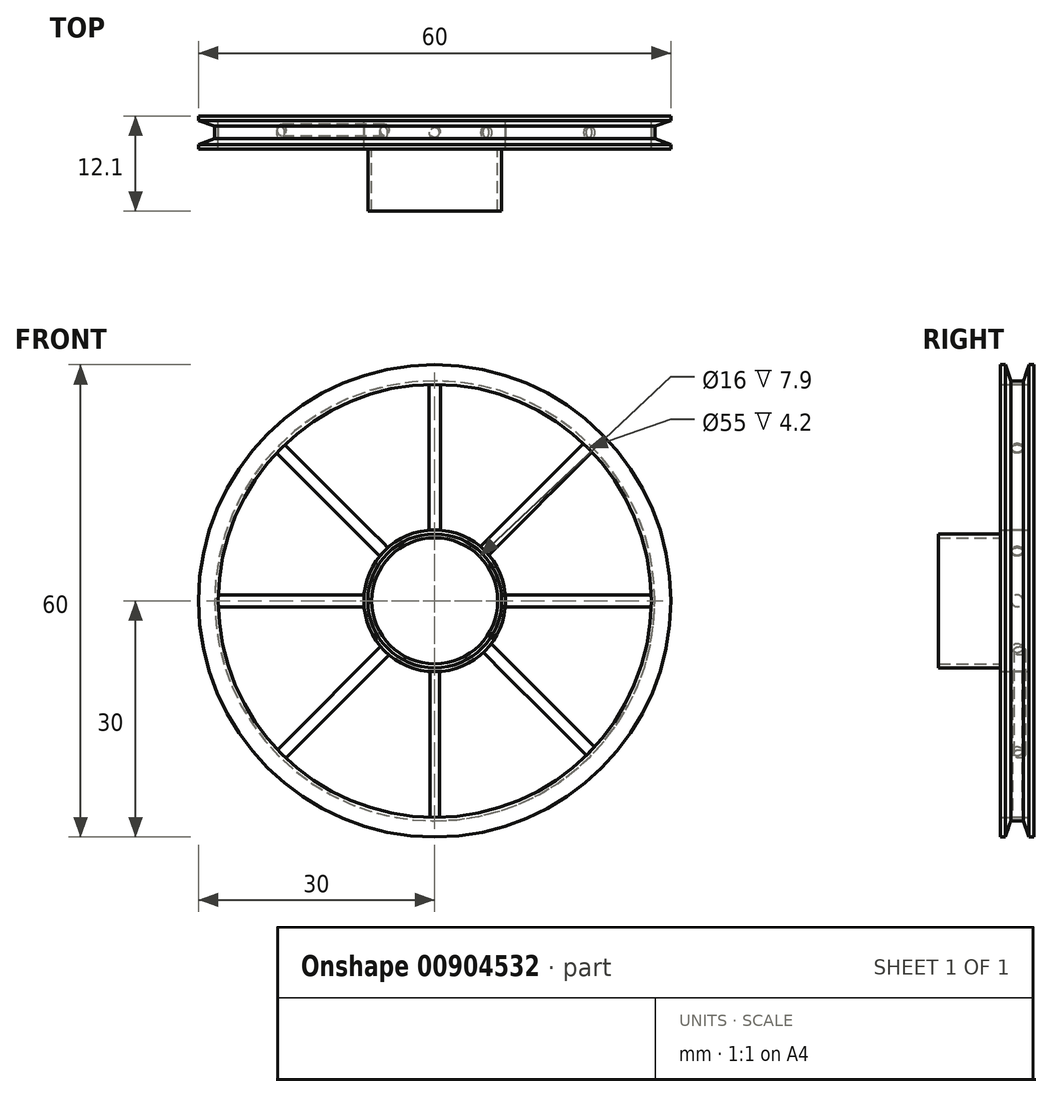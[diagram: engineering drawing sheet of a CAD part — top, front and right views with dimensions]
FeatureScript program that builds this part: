
annotation { "Feature Type Name" : "Feature", "Feature Type Description" : "" }
export const myFeature = defineFeature(function(context is Context, id is Id, definition is map)
    precondition{}
    {
        {
            var Q0;
            Q0=qCreatedBy(makeId("Front.planeOp"),FACE);
            var sketch = newSketch(context, id + "F0", { "sketchPlane" : qUnion([Q0])});
            skCircle(sketch, "E0", {"center": v(0, 0) * mm, "radius": 30 * mm});
            skCircle(sketch, "E1", {"center": v(0, 0) * mm, "radius": 27.5 * mm});
            skSolve(sketch);
        }
        {
            var Q0;
            Q0=qSketchRegion(id+"F0",true);
            extrude(context, id + "F1", {"entities" : qUnion([Q0]), "depth" : 2.1 * mm, "offsetDistance" : 25 * mm});
        }
        {
            var Q0;
            Q0=makeQuery(id+"F1.opExtrude","SWEPT_BODY",BODY,{"disambiguationData":[OSD([sQuery(id+"F0.wireOp",EDGE,"E0"),sQuery(id+"F0.wireOp",EDGE,"E1")])]});
            var Q1;
            Q1=qCreatedBy(makeId("Front.planeOp"),FACE);
            mirror(context, id + "F2", {"operationType" : NewBodyOperationType.ADD, "entities" : qUnion([Q0]), "mirrorPlane" : qUnion([Q1])});
        }
        {
            var Q0;
            Q0=qCreatedBy(makeId("Front.planeOp"),FACE);
            var sketch = newSketch(context, id + "F3", { "sketchPlane" : qUnion([Q0])});
            skCircle(sketch, "E2", {"center": v(0, 0) * mm, "radius": 8 * mm});
            skCircle(sketch, "E3", {"center": v(0, 0) * mm, "radius": 8.5 * mm});
            skSolve(sketch);
        }
        {
            var Q0;
            Q0=qSketchRegion(id+"F3",true);
            extrude(context, id + "F4", {"entities" : qUnion([Q0]), "depth" : 10 * mm, "offsetDistance" : 25 * mm});
        }
        {
            var Q0;
            Q0=qCreatedBy(makeId("Front.planeOp"),FACE);
            var sketch = newSketch(context, id + "F5", { "sketchPlane" : qUnion([Q0])});
            skCircle(sketch, "E4", {"center": v(0, 0) * mm, "radius": 9 * mm});
            skSolve(sketch);
        }
        {
            var Q0;
            Q0=makeQuery(id+"F5.imprint","IMPRINT",FACE,{"disambiguationData":[TD([[makeQuery(id+"F5.imprint","IMPRINT",EDGE,{"derivedFrom":sQuery(id+"F5.wireOp",EDGE,"E4")}),1.0]])]});
            extrude(context, id + "F6", {"entities" : qUnion([Q0]), "operationType" : NewBodyOperationType.ADD, "depth" : 2.1 * mm, "offsetDistance" : 25 * mm});
        }
        {
            var Q0;
            Q0=qCreatedBy(makeId("Front.planeOp"),FACE);
            var sketch = newSketch(context, id + "F7", { "sketchPlane" : qUnion([Q0])});
            skCircle(sketch, "E5", {"center": v(0, 0) * mm, "radius": 9 * mm});
            skSolve(sketch);
        }
        {
            var Q0;
            Q0=qSketchRegion(id+"F7",true);
            extrude(context, id + "F8", {"entities" : qUnion([Q0]), "operationType" : NewBodyOperationType.ADD, "oppositeDirection" : true, "depth" : 2.1 * mm, "offsetDistance" : 25 * mm});
        }
        {
            var Q0;
            Q0=qCreatedBy(makeId("Right.planeOp"),FACE);
            var sketch = newSketch(context, id + "F9", { "sketchPlane" : qUnion([Q0])});
            skLineSegment(sketch, "E6", {"start": v(1.7, -30.55) * mm, "end": v(-1.7, -30.55) * mm});
            skLineSegment(sketch, "E7", {"start": v(-1.7, -30.55) * mm, "end": v(-0.8, -27.95) * mm});
            skLineSegment(sketch, "E8", {"start": v(-0.8, -27.95) * mm, "end": v(0.8, -27.95) * mm});
            skLineSegment(sketch, "E9", {"start": v(0.8, -27.95) * mm, "end": v(1.7, -30.55) * mm});
            skLineSegment(sketch, "E10", {"start": v(0, -27.95) * mm, "end": v(0, -30.55) * mm});
            skLineSegment(sketch, "E11", {"start": v(0, 0) * mm, "end": v(-3.18, 0) * mm});
            skSolve(sketch);
        }
        {
            var Q0;
            {var subQ0=sQuery(id+"F9.wireOp",EDGE,"E7");Q0=makeQuery(id+"F9.imprint","IMPRINT",FACE,{"disambiguationData":[TD([[makeQuery(id+"F9.imprint","IMPRINT",EDGE,{"derivedFrom":subQ0}),-1.0]])]});}
            var Q1;
            {var subQ0=sQuery(id+"F9.wireOp",EDGE,"E9");Q1=makeQuery(id+"F9.imprint","IMPRINT",FACE,{"disambiguationData":[TD([[makeQuery(id+"F9.imprint","IMPRINT",EDGE,{"derivedFrom":subQ0}),-1.0]])]});}
            var Q2;
            Q2=sQuery(id+"F9.wireOp",EDGE,"E11");
            revolve(context, id + "F10", {"operationType" : NewBodyOperationType.REMOVE, "surfaceOperationType" : NewSurfaceOperationType.NEW, "entities" : qUnion([Q0, Q1]), "axis" : qUnion([Q2]), "revolveType" : RevolveType.FULL});
        }
        {
            var Q0;
            Q0=qCreatedBy(makeId("Front.planeOp"),FACE);
            var sketch = newSketch(context, id + "F11", { "sketchPlane" : qUnion([Q0])});
            skCircle(sketch, "E12", {"center": v(0, 0) * mm, "radius": 27.5 * mm, "construction": true});
            skCircle(sketch, "E13", {"center": v(0, 0) * mm, "radius": 9 * mm, "construction": true});
            skLineSegment(sketch, "E14", {"start": v(9, 0) * mm, "end": v(27.5, 0) * mm});
            skLineSegment(sketch, "E15", {"start": v(0, 9) * mm, "end": v(0, 27.5) * mm});
            skLineSegment(sketch, "E16", {"start": v(-9, 0) * mm, "end": v(-27.5, 0) * mm});
            skLineSegment(sketch, "E17", {"start": v(0, -9) * mm, "end": v(0, -27.5) * mm});
            skLineSegment(sketch, "E18", {"start": v(6.81, -5.88) * mm, "end": v(19.9, -18.97) * mm});
            skLineSegment(sketch, "E19", {"start": v(-6.71, -6) * mm, "end": v(-19.8, -19.08) * mm});
            skLineSegment(sketch, "E20", {"start": v(-6.55, 6.18) * mm, "end": v(-19.63, 19.26) * mm});
            skLineSegment(sketch, "E21", {"start": v(6.3, 6.42) * mm, "end": v(19.39, 19.5) * mm});
            skSolve(sketch);
        }
        {
            var Q0;
            Q0=sQuery(id+"F11.wireOp",EDGE,"E14");
            var Q1;
            Q1=sQuery(id+"F11.wireOp",VERTEX,"E14.start");
            cPlane(context, id + "F12", {"entities" : qUnion([Q0, Q1]), "cplaneType" : CPlaneType.LINE_POINT, "offset" : 25 * mm, "width" : 150 * mm, "height" : 150 * mm});
        }
        {
            var Q0;
            Q0=qCreatedBy(id+"F12.planeOp",FACE);
            var sketch = newSketch(context, id + "F13", { "sketchPlane" : qUnion([Q0])});
            skCircle(sketch, "E22", {"center": v(0, 0) * mm, "radius": 0.75 * mm});
            skSolve(sketch);
        }
        {
            var Q0;
            Q0=makeQuery(id+"F13.imprint","IMPRINT",FACE,{"disambiguationData":[TD([[makeQuery(id+"F13.imprint","IMPRINT",EDGE,{"derivedFrom":sQuery(id+"F13.wireOp",EDGE,"E22")}),1.0]])]});
            var Q1;
            Q1=sQuery(id+"F11.wireOp",EDGE,"E14");
            sweep(context, id + "F14", {"profiles" : qUnion([Q0]), "path" : qUnion([Q1])});
        }
        {
            var Q0;
            Q0=sQuery(id+"F11.wireOp",EDGE,"E21");
            var Q1;
            Q1=sQuery(id+"F11.wireOp",VERTEX,"E21.start");
            cPlane(context, id + "F15", {"entities" : qUnion([Q0, Q1]), "cplaneType" : CPlaneType.LINE_POINT, "offset" : 25 * mm, "width" : 150 * mm, "height" : 150 * mm});
        }
        {
            var Q0;
            Q0=sQuery(id+"F11.wireOp",EDGE,"E15");
            var Q1;
            Q1=sQuery(id+"F11.wireOp",VERTEX,"E15.start");
            cPlane(context, id + "F16", {"entities" : qUnion([Q0, Q1]), "cplaneType" : CPlaneType.LINE_POINT, "offset" : 25 * mm, "width" : 150 * mm, "height" : 150 * mm});
        }
        {
            var Q0;
            Q0=sQuery(id+"F11.wireOp",EDGE,"E20");
            var Q1;
            Q1=sQuery(id+"F11.wireOp",VERTEX,"E20.start");
            cPlane(context, id + "F17", {"entities" : qUnion([Q0, Q1]), "cplaneType" : CPlaneType.LINE_POINT, "offset" : 25 * mm, "width" : 150 * mm, "height" : 150 * mm});
        }
        {
            var Q0;
            Q0=sQuery(id+"F11.wireOp",EDGE,"E16");
            var Q1;
            Q1=sQuery(id+"F11.wireOp",VERTEX,"E16.start");
            cPlane(context, id + "F18", {"entities" : qUnion([Q0, Q1]), "cplaneType" : CPlaneType.LINE_POINT, "offset" : 25 * mm, "width" : 150 * mm, "height" : 150 * mm});
        }
        {
            var Q0;
            Q0=sQuery(id+"F11.wireOp",VERTEX,"E19.start");
            var Q1;
            Q1=sQuery(id+"F11.wireOp",EDGE,"E19");
            cPlane(context, id + "F19", {"entities" : qUnion([Q0, Q1]), "cplaneType" : CPlaneType.LINE_POINT, "offset" : 25 * mm, "width" : 150 * mm, "height" : 150 * mm});
        }
        {
            var Q0;
            Q0=sQuery(id+"F11.wireOp",VERTEX,"E17.start");
            var Q1;
            Q1=sQuery(id+"F11.wireOp",EDGE,"E17");
            cPlane(context, id + "F20", {"entities" : qUnion([Q0, Q1]), "cplaneType" : CPlaneType.LINE_POINT, "offset" : 25 * mm, "width" : 150 * mm, "height" : 150 * mm});
        }
        {
            var Q0;
            Q0=sQuery(id+"F11.wireOp",VERTEX,"E18.start");
            var Q1;
            Q1=sQuery(id+"F11.wireOp",EDGE,"E18");
            cPlane(context, id + "F21", {"entities" : qUnion([Q0, Q1]), "cplaneType" : CPlaneType.LINE_POINT, "offset" : 25 * mm, "width" : 150 * mm, "height" : 150 * mm});
        }
        {
            var Q0;
            Q0=qCreatedBy(id+"F15.planeOp",FACE);
            var sketch = newSketch(context, id + "F22", { "sketchPlane" : qUnion([Q0])});
            skCircle(sketch, "E23", {"center": v(0, 0) * mm, "radius": 0.75 * mm});
            skSolve(sketch);
        }
        {
            var Q0;
            Q0=qCreatedBy(id+"F16.planeOp",FACE);
            var sketch = newSketch(context, id + "F23", { "sketchPlane" : qUnion([Q0])});
            skCircle(sketch, "E24", {"center": v(0, 0) * mm, "radius": 0.75 * mm});
            skSolve(sketch);
        }
        {
            var Q0;
            Q0=qCreatedBy(id+"F17.planeOp",FACE);
            var sketch = newSketch(context, id + "F24", { "sketchPlane" : qUnion([Q0])});
            skCircle(sketch, "E25", {"center": v(0, -0.2) * mm, "radius": 0.75 * mm});
            skSolve(sketch);
        }
        {
            var Q0;
            Q0=qCreatedBy(id+"F18.planeOp",FACE);
            var sketch = newSketch(context, id + "F25", { "sketchPlane" : qUnion([Q0])});
            skCircle(sketch, "E26", {"center": v(0, 0) * mm, "radius": 0.75 * mm});
            skSolve(sketch);
        }
        {
            var Q0;
            Q0=qCreatedBy(id+"F19.planeOp",FACE);
            var sketch = newSketch(context, id + "F26", { "sketchPlane" : qUnion([Q0])});
            skCircle(sketch, "E27", {"center": v(-0.31, 0) * mm, "radius": 0.75 * mm});
            skSolve(sketch);
        }
        {
            var Q0;
            Q0=qCreatedBy(id+"F20.planeOp",FACE);
            var sketch = newSketch(context, id + "F27", { "sketchPlane" : qUnion([Q0])});
            skCircle(sketch, "E28", {"center": v(0, 0) * mm, "radius": 0.6 * mm});
            skSolve(sketch);
        }
        {
            var Q0;
            Q0=qCreatedBy(id+"F21.planeOp",FACE);
            var sketch = newSketch(context, id + "F28", { "sketchPlane" : qUnion([Q0])});
            skCircle(sketch, "E29", {"center": v(0, 0.48) * mm, "radius": 0.75 * mm});
            skSolve(sketch);
        }
        {
            var Q0;
            Q0=makeQuery(id+"F28.imprint","IMPRINT",FACE,{"disambiguationData":[TD([[makeQuery(id+"F28.imprint","IMPRINT",EDGE,{"derivedFrom":sQuery(id+"F28.wireOp",EDGE,"E29")}),1.0]])]});
            var Q1;
            Q1=sQuery(id+"F11.wireOp",EDGE,"E18");
            sweep(context, id + "F29", {"profiles" : qUnion([Q0]), "path" : qUnion([Q1])});
        }
        {
            var Q0;
            Q0=makeQuery(id+"F27.imprint","IMPRINT",FACE,{"disambiguationData":[TD([[makeQuery(id+"F27.imprint","IMPRINT",EDGE,{"derivedFrom":sQuery(id+"F27.wireOp",EDGE,"E28")}),1.0]])]});
            var Q1;
            Q1=sQuery(id+"F11.wireOp",EDGE,"E17");
            sweep(context, id + "F30", {"profiles" : qUnion([Q0]), "path" : qUnion([Q1])});
        }
        {
            var Q0;
            Q0=makeQuery(id+"F26.imprint","IMPRINT",FACE,{"disambiguationData":[TD([[makeQuery(id+"F26.imprint","IMPRINT",EDGE,{"derivedFrom":sQuery(id+"F26.wireOp",EDGE,"E27")}),1.0]])]});
            var Q1;
            Q1=sQuery(id+"F11.wireOp",EDGE,"E19");
            sweep(context, id + "F31", {"profiles" : qUnion([Q0]), "path" : qUnion([Q1])});
        }
        {
            var Q0;
            Q0=makeQuery(id+"F25.imprint","IMPRINT",FACE,{"disambiguationData":[TD([[makeQuery(id+"F25.imprint","IMPRINT",EDGE,{"derivedFrom":sQuery(id+"F25.wireOp",EDGE,"E26")}),1.0]])]});
            var Q1;
            Q1=sQuery(id+"F11.wireOp",EDGE,"E16");
            sweep(context, id + "F32", {"profiles" : qUnion([Q0]), "path" : qUnion([Q1])});
        }
        {
            var Q0;
            Q0=makeQuery(id+"F24.imprint","IMPRINT",FACE,{"disambiguationData":[TD([[makeQuery(id+"F24.imprint","IMPRINT",EDGE,{"derivedFrom":sQuery(id+"F24.wireOp",EDGE,"E25")}),1.0]])]});
            var Q1;
            Q1=sQuery(id+"F11.wireOp",EDGE,"E20");
            sweep(context, id + "F33", {"profiles" : qUnion([Q0]), "path" : qUnion([Q1])});
        }
        {
            var Q0;
            Q0=makeQuery(id+"F23.imprint","IMPRINT",FACE,{"disambiguationData":[TD([[makeQuery(id+"F23.imprint","IMPRINT",EDGE,{"derivedFrom":sQuery(id+"F23.wireOp",EDGE,"E24")}),1.0]])]});
            var Q1;
            Q1=sQuery(id+"F11.wireOp",EDGE,"E15");
            sweep(context, id + "F34", {"profiles" : qUnion([Q0]), "path" : qUnion([Q1])});
        }
        {
            var Q0;
            Q0=makeQuery(id+"F22.imprint","IMPRINT",FACE,{"disambiguationData":[TD([[makeQuery(id+"F22.imprint","IMPRINT",EDGE,{"derivedFrom":sQuery(id+"F22.wireOp",EDGE,"E23")}),1.0]])]});
            var Q1;
            Q1=sQuery(id+"F11.wireOp",EDGE,"E21");
            sweep(context, id + "F35", {"profiles" : qUnion([Q0]), "path" : qUnion([Q1])});
        }
    });
